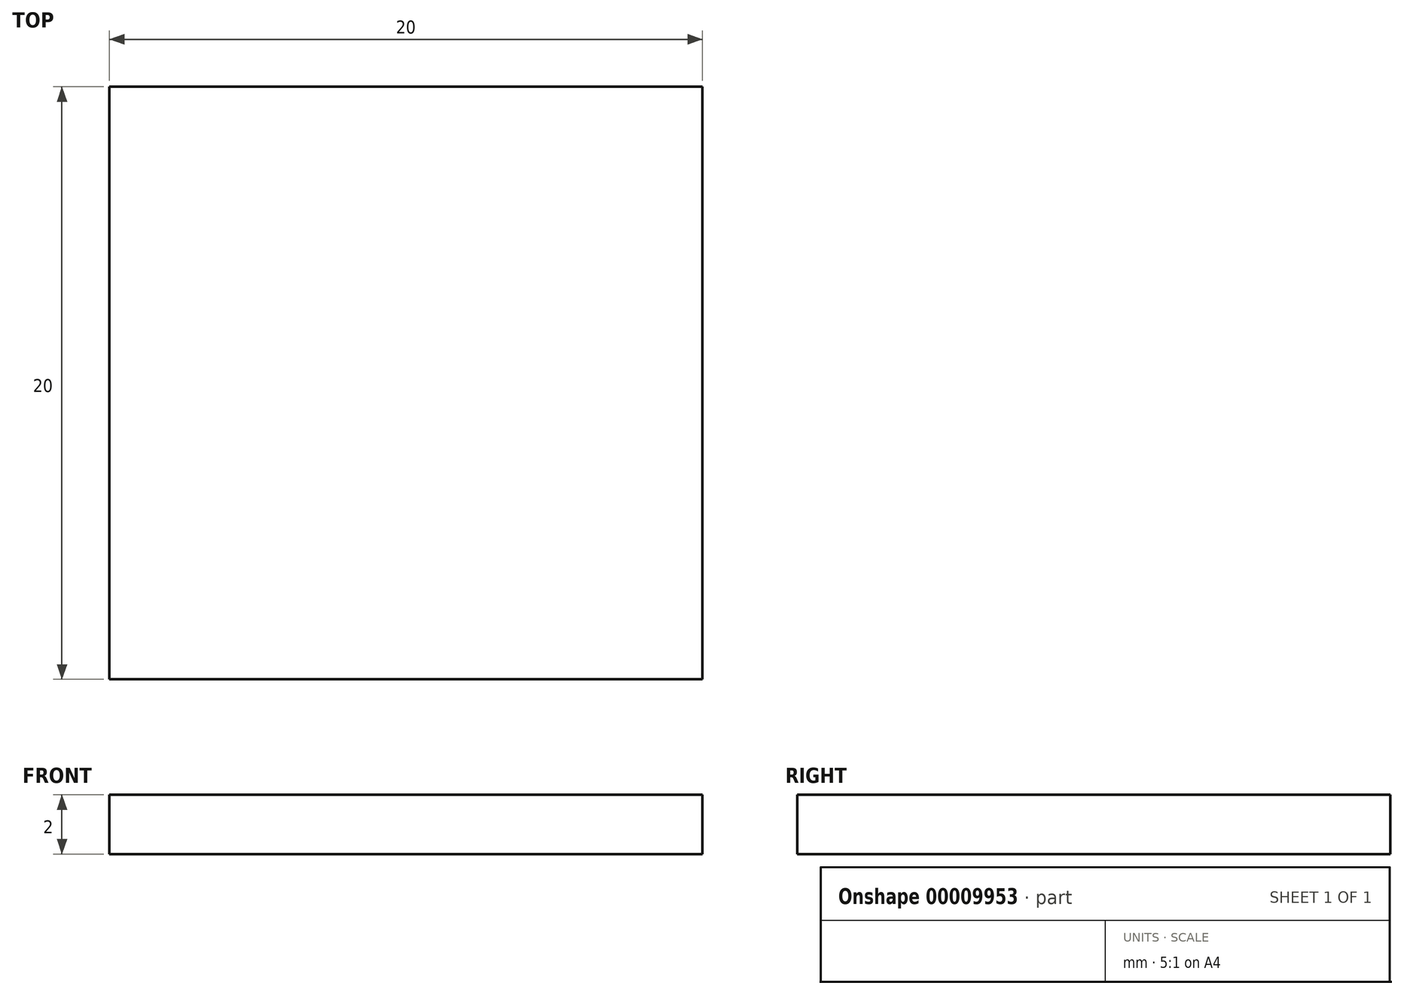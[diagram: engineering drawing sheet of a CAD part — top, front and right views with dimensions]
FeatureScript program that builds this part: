
annotation { "Feature Type Name" : "Feature", "Feature Type Description" : "" }
export const myFeature = defineFeature(function(context is Context, id is Id, definition is map)
    precondition{}
    {
        {
            var Q0;
            Q0=qCreatedBy(makeId("Top.planeOp"),FACE);
            var sketch = newSketch(context, id + "F0", { "sketchPlane" : qUnion([Q0])});
            skLineSegment(sketch, "E0.bottom", {"start": v(-0.27, 11.84) * mm, "end": v(19.73, 11.84) * mm});
            skLineSegment(sketch, "E0.top", {"start": v(-0.27, -8.16) * mm, "end": v(19.73, -8.16) * mm});
            skLineSegment(sketch, "E0.left", {"start": v(-0.27, 11.84) * mm, "end": v(-0.27, -8.16) * mm});
            skLineSegment(sketch, "E0.right", {"start": v(19.73, 11.84) * mm, "end": v(19.73, -8.16) * mm});
            skSolve(sketch);
        }
        {
            var Q0;
            Q0 = qSketchRegion(id + "F0", true);
            extrude(context, id + "F1", {"entities" : qUnion([Q0]), "depth" : 2 * mm});
        }
    });
